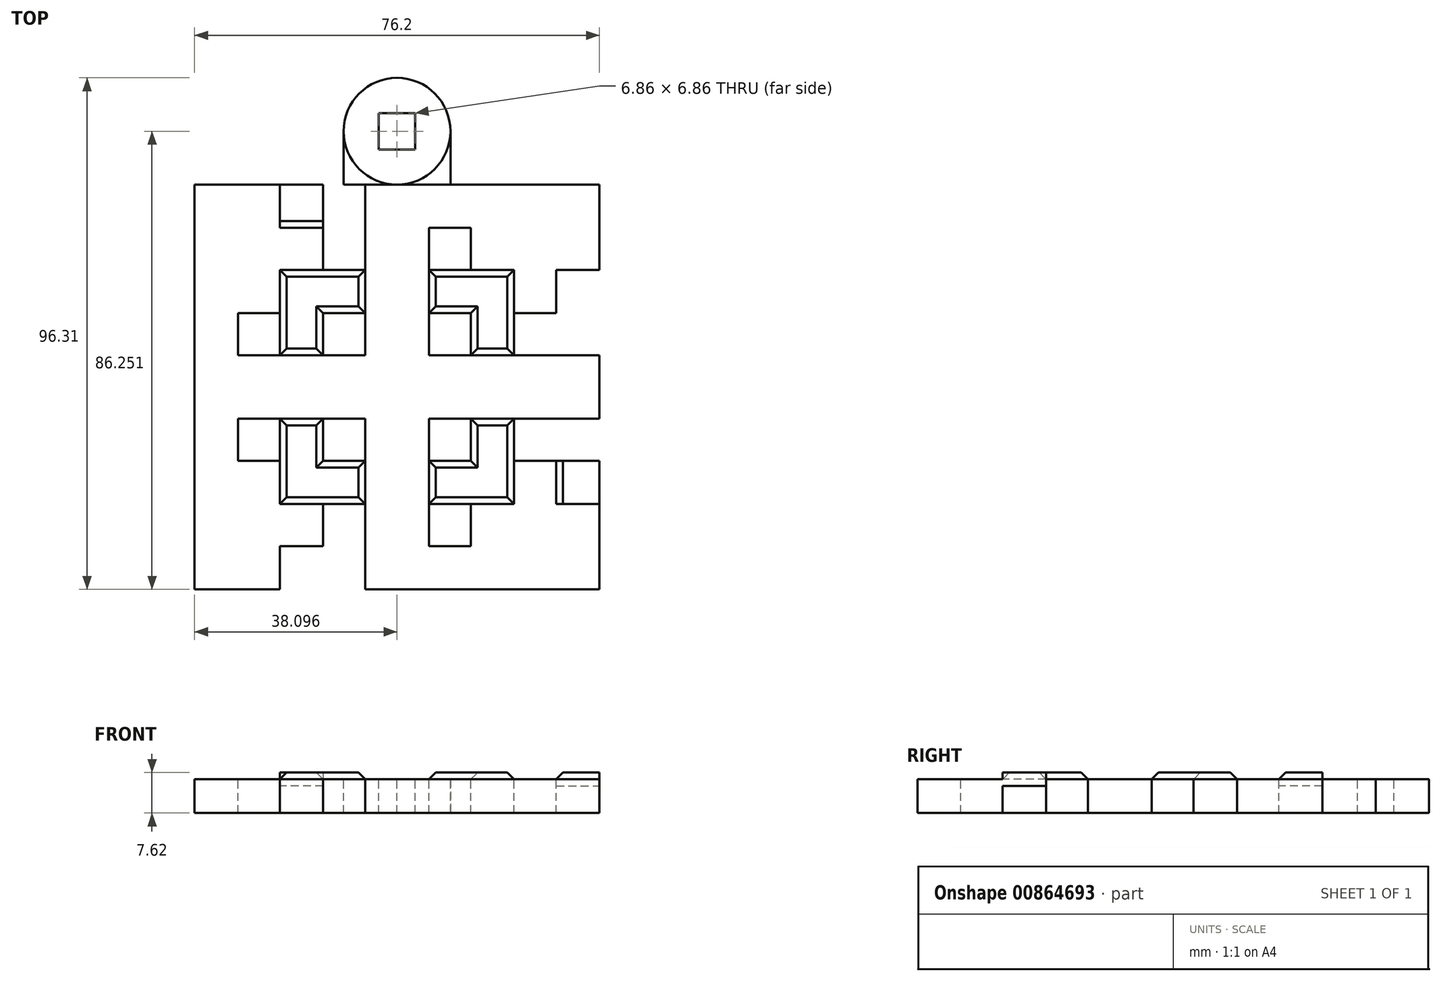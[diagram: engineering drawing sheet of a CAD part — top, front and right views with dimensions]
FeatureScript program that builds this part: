
annotation { "Feature Type Name" : "Feature", "Feature Type Description" : "" }
export const myFeature = defineFeature(function(context is Context, id is Id, definition is map)
    precondition{}
    {
        {
            var Q0;
            Q0=qCreatedBy(makeId("Top.planeOp"),FACE);
            var sketch = newSketch(context, id + "F0", { "sketchPlane" : qUnion([Q0])});
            skLineSegment(sketch, "E0.bottom", {"start": v(-34.48, 49.13) * mm, "end": v(41.72, 49.13) * mm});
            skLineSegment(sketch, "E0.top", {"start": v(-34.48, -27.07) * mm, "end": v(41.72, -27.07) * mm});
            skLineSegment(sketch, "E0.left", {"start": v(-34.48, 49.13) * mm, "end": v(-34.48, -27.07) * mm});
            skLineSegment(sketch, "E0.right", {"start": v(41.72, 49.13) * mm, "end": v(41.72, -27.07) * mm});
            skCircle(sketch, "E1", {"center": v(3.62, 59.18) * mm, "radius": 10.06 * mm});
            skLineSegment(sketch, "E2", {"start": v(3.62, -27.07) * mm, "end": v(3.62, 49.13) * mm, "construction": true});
            skPoint(sketch, "E3", {"position": v(3.62, 49.13) * mm});
            skSolve(sketch);
        }
        {
            var Q0;
            Q0 = qSketchRegion(id + "F0", true);
            extrude(context, id + "F1", {"entities" : qUnion([Q0]), "depth" : 6.35 * mm, "offsetDistance" : 25.4 * mm});
        }
        {
            var Q0;
            Q0=makeQuery(id+"F1.opExtrude","CAP_FACE",FACE,{"disambiguationData":[OSD([sQuery(id+"F0.wireOp",EDGE,"E0.bottom"),sQuery(id+"F0.wireOp",EDGE,"E0.top"),sQuery(id+"F0.wireOp",EDGE,"E0.left"),sQuery(id+"F0.wireOp",EDGE,"E0.right")])],"isStart":false});
            var sketch = newSketch(context, id + "F2", { "sketchPlane" : qUnion([Q0])});
            skLineSegment(sketch, "E4.bottom", {"start": v(-34.48, 5.04) * mm, "end": v(41.72, 5.04) * mm});
            skLineSegment(sketch, "E4.top", {"start": v(-34.48, 17.01) * mm, "end": v(41.72, 17.01) * mm});
            skLineSegment(sketch, "E4.left", {"start": v(-34.48, 5.04) * mm, "end": v(-34.48, 17.01) * mm});
            skLineSegment(sketch, "E4.right", {"start": v(41.72, 5.04) * mm, "end": v(41.72, 17.01) * mm});
            skLineSegment(sketch, "E5.bottom", {"start": v(-34.48, 49.13) * mm, "end": v(-2.37, 49.13) * mm});
            skLineSegment(sketch, "E5.top", {"start": v(-34.48, -27.07) * mm, "end": v(-2.37, -27.07) * mm});
            skLineSegment(sketch, "E5.left", {"start": v(-34.48, 49.13) * mm, "end": v(-34.48, 17.01) * mm});
            skLineSegment(sketch, "E5.right", {"start": v(41.72, 49.13) * mm, "end": v(41.72, 17.01) * mm});
            skLineSegment(sketch, "E6", {"start": v(41.72, 17.01) * mm, "end": v(41.72, 5.04) * mm});
            skLineSegment(sketch, "E7", {"start": v(41.72, 5.04) * mm, "end": v(41.72, -27.07) * mm});
            skLineSegment(sketch, "E8.bottom", {"start": v(-2.37, 49.13) * mm, "end": v(9.6, 49.13) * mm});
            skLineSegment(sketch, "E8.top", {"start": v(-2.37, -27.07) * mm, "end": v(9.6, -27.07) * mm});
            skLineSegment(sketch, "E8.left", {"start": v(-2.37, 49.13) * mm, "end": v(-2.37, 49.13) * mm});
            skLineSegment(sketch, "E8.right", {"start": v(9.6, 49.13) * mm, "end": v(9.6, -27.07) * mm});
            skLineSegment(sketch, "E9", {"start": v(-2.37, 49.13) * mm, "end": v(-2.37, -27.07) * mm});
            skLineSegment(sketch, "E10", {"start": v(9.6, 49.13) * mm, "end": v(41.72, 49.13) * mm});
            skLineSegment(sketch, "E11", {"start": v(9.6, -27.07) * mm, "end": v(41.72, -27.07) * mm});
            skPoint(sketch, "E12.oppositeSnap0", {"position": v(25.66, 49.13) * mm});
            skLineSegment(sketch, "E12.bottom", {"start": v(-18.43, 49.13) * mm, "end": v(25.66, 49.13) * mm});
            skLineSegment(sketch, "E12.top", {"start": v(-18.43, 40.98) * mm, "end": v(25.66, 40.98) * mm});
            skLineSegment(sketch, "E12.left", {"start": v(-18.43, 49.13) * mm, "end": v(-18.43, 40.98) * mm});
            skLineSegment(sketch, "E12.right", {"start": v(25.66, 49.13) * mm, "end": v(25.66, 40.98) * mm});
            skPoint(sketch, "E13.oppositeSnap0", {"position": v(-18.43, -27.07) * mm});
            skLineSegment(sketch, "E13.bottom", {"start": v(25.66, -27.07) * mm, "end": v(-18.43, -27.07) * mm});
            skLineSegment(sketch, "E13.top", {"start": v(25.66, -18.92) * mm, "end": v(-18.43, -18.92) * mm});
            skLineSegment(sketch, "E13.left", {"start": v(25.66, -27.07) * mm, "end": v(25.66, -18.92) * mm});
            skLineSegment(sketch, "E13.right", {"start": v(-18.43, -27.07) * mm, "end": v(-18.43, -18.92) * mm});
            skPoint(sketch, "E14.oppositeSnap0", {"position": v(41.72, 33.07) * mm});
            skLineSegment(sketch, "E14.bottom", {"start": v(41.72, -11.02) * mm, "end": v(33.57, -11.02) * mm});
            skLineSegment(sketch, "E14.top", {"start": v(41.72, 33.07) * mm, "end": v(33.57, 33.07) * mm});
            skLineSegment(sketch, "E14.left", {"start": v(41.72, -11.02) * mm, "end": v(41.72, 33.07) * mm});
            skLineSegment(sketch, "E14.right", {"start": v(33.57, -11.02) * mm, "end": v(33.57, 33.07) * mm});
            skLineSegment(sketch, "E15", {"start": v(-34.48, 17.01) * mm, "end": v(-34.48, 5.04) * mm});
            skLineSegment(sketch, "E16", {"start": v(-34.48, 5.04) * mm, "end": v(-34.48, -27.07) * mm});
            skPoint(sketch, "E17.oppositeSnap0", {"position": v(-34.48, -11.02) * mm});
            skLineSegment(sketch, "E17.bottom", {"start": v(-34.48, 33.07) * mm, "end": v(-26.33, 33.07) * mm});
            skLineSegment(sketch, "E17.top", {"start": v(-34.48, -11.02) * mm, "end": v(-26.33, -11.02) * mm});
            skLineSegment(sketch, "E17.left", {"start": v(-34.48, 33.07) * mm, "end": v(-34.48, -11.02) * mm});
            skLineSegment(sketch, "E17.right", {"start": v(-26.33, 33.07) * mm, "end": v(-26.33, 24.92) * mm});
            skLineSegment(sketch, "E18.bottom", {"start": v(-18.43, 40.98) * mm, "end": v(-10.28, 40.98) * mm});
            skLineSegment(sketch, "E18.top", {"start": v(-18.43, 17.01) * mm, "end": v(-10.28, 17.01) * mm});
            skLineSegment(sketch, "E18.left", {"start": v(-18.43, 40.98) * mm, "end": v(-18.43, 17.01) * mm});
            skLineSegment(sketch, "E18.right", {"start": v(-10.28, 40.98) * mm, "end": v(-10.28, 17.01) * mm});
            skLineSegment(sketch, "E19.bottom", {"start": v(-26.33, 33.07) * mm, "end": v(-2.37, 33.07) * mm});
            skLineSegment(sketch, "E19.top", {"start": v(-26.33, 24.92) * mm, "end": v(-2.37, 24.92) * mm});
            skLineSegment(sketch, "E19.right", {"start": v(-2.37, 33.07) * mm, "end": v(-2.37, 24.92) * mm});
            skLineSegment(sketch, "E20", {"start": v(-26.33, 24.92) * mm, "end": v(-26.33, -11.02) * mm});
            skLineSegment(sketch, "E21.bottom", {"start": v(25.66, 40.98) * mm, "end": v(17.51, 40.98) * mm});
            skLineSegment(sketch, "E21.top", {"start": v(25.66, 17.01) * mm, "end": v(17.51, 17.01) * mm});
            skLineSegment(sketch, "E21.left", {"start": v(25.66, 40.98) * mm, "end": v(25.66, 17.01) * mm});
            skLineSegment(sketch, "E21.right", {"start": v(17.51, 40.98) * mm, "end": v(17.51, 17.01) * mm});
            skLineSegment(sketch, "E22.bottom", {"start": v(33.57, 33.07) * mm, "end": v(9.6, 33.07) * mm});
            skLineSegment(sketch, "E22.top", {"start": v(33.57, 24.92) * mm, "end": v(9.6, 24.92) * mm});
            skLineSegment(sketch, "E22.left", {"start": v(33.57, 33.07) * mm, "end": v(33.57, 24.92) * mm});
            skLineSegment(sketch, "E22.right", {"start": v(9.6, 33.07) * mm, "end": v(9.6, 24.92) * mm});
            skPoint(sketch, "E23.oppositeSnap0", {"position": v(-10.28, 29) * mm});
            skLineSegment(sketch, "E23.bottom", {"start": v(-18.43, -18.92) * mm, "end": v(-10.28, -18.92) * mm});
            skLineSegment(sketch, "E23.top", {"start": v(-18.43, 5.04) * mm, "end": v(-10.28, 5.04) * mm});
            skLineSegment(sketch, "E23.left", {"start": v(-18.43, -18.92) * mm, "end": v(-18.43, 5.04) * mm});
            skLineSegment(sketch, "E23.right", {"start": v(-10.28, -18.92) * mm, "end": v(-10.28, 5.04) * mm});
            skLineSegment(sketch, "E24.bottom", {"start": v(25.66, -18.92) * mm, "end": v(17.51, -18.92) * mm});
            skLineSegment(sketch, "E24.top", {"start": v(25.66, 5.04) * mm, "end": v(17.51, 5.04) * mm});
            skLineSegment(sketch, "E24.left", {"start": v(25.66, -18.92) * mm, "end": v(25.66, 5.04) * mm});
            skLineSegment(sketch, "E24.right", {"start": v(17.51, -18.92) * mm, "end": v(17.51, 5.04) * mm});
            skLineSegment(sketch, "E25.bottom", {"start": v(-26.33, -11.02) * mm, "end": v(-2.37, -11.02) * mm});
            skLineSegment(sketch, "E25.top", {"start": v(-26.33, -2.87) * mm, "end": v(-2.37, -2.87) * mm});
            skLineSegment(sketch, "E25.left", {"start": v(-26.33, -11.02) * mm, "end": v(-26.33, -2.87) * mm});
            skLineSegment(sketch, "E25.right", {"start": v(-2.37, -11.02) * mm, "end": v(-2.37, -2.87) * mm});
            skLineSegment(sketch, "E26.bottom", {"start": v(9.6, -11.02) * mm, "end": v(33.57, -11.02) * mm});
            skLineSegment(sketch, "E26.top", {"start": v(9.6, -2.87) * mm, "end": v(33.57, -2.87) * mm});
            skLineSegment(sketch, "E26.left", {"start": v(9.6, -11.02) * mm, "end": v(9.6, -2.87) * mm});
            skLineSegment(sketch, "E26.right", {"start": v(33.57, -11.02) * mm, "end": v(33.57, -2.87) * mm});
            skLineSegment(sketch, "E27.bottom", {"start": v(-18.43, 49.13) * mm, "end": v(-10.28, 49.13) * mm});
            skLineSegment(sketch, "E27.right", {"start": v(-10.28, 49.13) * mm, "end": v(-10.28, 40.98) * mm});
            skLineSegment(sketch, "E28.bottom", {"start": v(17.51, 40.98) * mm, "end": v(25.66, 40.98) * mm});
            skLineSegment(sketch, "E28.top", {"start": v(17.51, 49.13) * mm, "end": v(25.66, 49.13) * mm});
            skLineSegment(sketch, "E28.left", {"start": v(17.51, 40.98) * mm, "end": v(17.51, 49.13) * mm});
            skLineSegment(sketch, "E28.right", {"start": v(25.66, 40.98) * mm, "end": v(25.66, 49.13) * mm});
            skLineSegment(sketch, "E29.bottom", {"start": v(33.57, 24.92) * mm, "end": v(41.72, 24.92) * mm});
            skLineSegment(sketch, "E29.top", {"start": v(33.57, 17.01) * mm, "end": v(41.72, 17.01) * mm});
            skLineSegment(sketch, "E29.left", {"start": v(33.57, 24.92) * mm, "end": v(33.57, 17.01) * mm});
            skLineSegment(sketch, "E29.right", {"start": v(41.72, 24.92) * mm, "end": v(41.72, 17.01) * mm});
            skLineSegment(sketch, "E30.bottom", {"start": v(-26.33, 24.92) * mm, "end": v(-34.48, 24.92) * mm});
            skLineSegment(sketch, "E30.top", {"start": v(-26.33, 33.07) * mm, "end": v(-34.48, 33.07) * mm});
            skLineSegment(sketch, "E30.left", {"start": v(-26.33, 24.92) * mm, "end": v(-26.33, 33.07) * mm});
            skLineSegment(sketch, "E30.right", {"start": v(-34.48, 24.92) * mm, "end": v(-34.48, 33.07) * mm});
            skLineSegment(sketch, "E31.top", {"start": v(-34.48, -2.87) * mm, "end": v(-26.33, -2.87) * mm});
            skLineSegment(sketch, "E31.left", {"start": v(-34.48, -11.02) * mm, "end": v(-34.48, -2.87) * mm});
            skLineSegment(sketch, "E32.top", {"start": v(-18.43, -27.07) * mm, "end": v(-10.28, -27.07) * mm});
            skLineSegment(sketch, "E32.left", {"start": v(-18.43, -18.92) * mm, "end": v(-18.43, -27.07) * mm});
            skLineSegment(sketch, "E32.right", {"start": v(-10.28, -18.92) * mm, "end": v(-10.28, -27.07) * mm});
            skLineSegment(sketch, "E33.bottom", {"start": v(17.51, -18.92) * mm, "end": v(25.66, -18.92) * mm});
            skLineSegment(sketch, "E33.top", {"start": v(17.51, -27.07) * mm, "end": v(25.66, -27.07) * mm});
            skLineSegment(sketch, "E33.left", {"start": v(17.51, -18.92) * mm, "end": v(17.51, -27.07) * mm});
            skLineSegment(sketch, "E33.right", {"start": v(25.66, -18.92) * mm, "end": v(25.66, -27.07) * mm});
            skLineSegment(sketch, "E34.bottom", {"start": v(33.57, -11.02) * mm, "end": v(41.72, -11.02) * mm});
            skLineSegment(sketch, "E34.top", {"start": v(33.57, -2.87) * mm, "end": v(41.72, -2.87) * mm});
            skLineSegment(sketch, "E34.right", {"start": v(41.72, -11.02) * mm, "end": v(41.72, -2.87) * mm});
            skSolve(sketch);
        }
        {
            var Q0;
            Q0=makeQuery(id+"F2.imprint","IMPRINT",FACE,{"disambiguationData":[TD([[makeQuery(id+"F2.imprint","IMPRINT",EDGE,{"derivedFrom":sQuery(id+"F2.wireOp",EDGE,"E5.bottom")}),-1.0]])]});
            var Q1;
            Q1=makeQuery(id+"F2.imprint","IMPRINT",FACE,{"disambiguationData":[TD([[makeQuery(id+"F2.imprint","IMPRINT",EDGE,{"derivedFrom":sQuery(id+"F2.wireOp",EDGE,"E5.right")}),-1.0]])]});
            var Q2;
            Q2=makeQuery(id+"F2.imprint","IMPRINT",FACE,{"disambiguationData":[TD([[makeQuery(id+"F2.imprint","IMPRINT",EDGE,{"derivedFrom":sQuery(id+"F2.wireOp",EDGE,"E7")}),-1.0]])]});
            var Q3;
            Q3=makeQuery(id+"F2.imprint","IMPRINT",FACE,{"disambiguationData":[TD([[makeQuery(id+"F2.imprint","IMPRINT",EDGE,{"derivedFrom":sQuery(id+"F2.wireOp",EDGE,"E5.top")}),1.0]])]});
            var Q4;
            {var subQ1=sQuery(id+"F2.wireOp",EDGE,"E4.bottom");var subQ3=sQuery(id+"F2.wireOp",EDGE,"E20");var subQ4=makeQuery(id+"F2.imprint","INTERSECT",VERTEX,{"derivedFrom":[subQ1,subQ3]});Q4=makeQuery(id+"F2.imprint","IMPRINT",FACE,{"disambiguationData":[TD([[makeQuery(id+"F2.imprint","IMPRINT",EDGE,{"disambiguationData":[TD([[subQ4,-1.0]])],"derivedFrom":subQ1}),-1.0]])]});}
            var Q5;
            {var subQ1=sQuery(id+"F2.wireOp",EDGE,"E4.top");var subQ3=sQuery(id+"F2.wireOp",EDGE,"E20");var subQ4=makeQuery(id+"F2.imprint","INTERSECT",VERTEX,{"derivedFrom":[subQ1,subQ3]});Q5=makeQuery(id+"F2.imprint","IMPRINT",FACE,{"disambiguationData":[TD([[makeQuery(id+"F2.imprint","IMPRINT",EDGE,{"disambiguationData":[TD([[subQ4,-1.0]])],"derivedFrom":subQ1}),1.0]])]});}
            var Q6;
            {var subQ1=sQuery(id+"F2.wireOp",EDGE,"E9");var subQ3=sQuery(id+"F2.wireOp",EDGE,"E12.top");var subQ4=makeQuery(id+"F2.imprint","INTERSECT",VERTEX,{"derivedFrom":[subQ1,subQ3]});Q6=makeQuery(id+"F2.imprint","IMPRINT",FACE,{"disambiguationData":[TD([[makeQuery(id+"F2.imprint","IMPRINT",EDGE,{"disambiguationData":[TD([[subQ4,-1.0]])],"derivedFrom":subQ1}),-1.0]])]});}
            var Q7;
            {var subQ1=sQuery(id+"F2.wireOp",EDGE,"E4.top");var subQ3=sQuery(id+"F2.wireOp",EDGE,"E9");var subQ4=makeQuery(id+"F2.imprint","INTERSECT",VERTEX,{"derivedFrom":[subQ1,subQ3]});Q7=makeQuery(id+"F2.imprint","IMPRINT",FACE,{"disambiguationData":[TD([[makeQuery(id+"F2.imprint","IMPRINT",EDGE,{"disambiguationData":[TD([[subQ4,1.0]])],"derivedFrom":subQ1}),1.0]])]});}
            var Q8;
            {var subQ1=sQuery(id+"F2.wireOp",EDGE,"E4.bottom");var subQ3=sQuery(id+"F2.wireOp",EDGE,"E9");var subQ4=makeQuery(id+"F2.imprint","INTERSECT",VERTEX,{"derivedFrom":[subQ1,subQ3]});Q8=makeQuery(id+"F2.imprint","IMPRINT",FACE,{"disambiguationData":[TD([[makeQuery(id+"F2.imprint","IMPRINT",EDGE,{"disambiguationData":[TD([[subQ4,1.0]])],"derivedFrom":subQ1}),-1.0]])]});}
            var Q9;
            {var subQ1=sQuery(id+"F2.wireOp",EDGE,"E9");var subQ3=sQuery(id+"F2.wireOp",EDGE,"E13.top");var subQ4=makeQuery(id+"F2.imprint","INTERSECT",VERTEX,{"derivedFrom":[subQ1,subQ3]});Q9=makeQuery(id+"F2.imprint","IMPRINT",FACE,{"disambiguationData":[TD([[makeQuery(id+"F2.imprint","IMPRINT",EDGE,{"disambiguationData":[TD([[subQ4,1.0]])],"derivedFrom":subQ1}),-1.0]])]});}
            var Q10;
            {var subQ1=sQuery(id+"F2.wireOp",EDGE,"E8.right");var subQ3=sQuery(id+"F2.wireOp",EDGE,"E13.top");var subQ4=makeQuery(id+"F2.imprint","INTERSECT",VERTEX,{"derivedFrom":[subQ1,subQ3]});Q10=makeQuery(id+"F2.imprint","IMPRINT",FACE,{"disambiguationData":[TD([[makeQuery(id+"F2.imprint","IMPRINT",EDGE,{"disambiguationData":[TD([[subQ4,1.0]])],"derivedFrom":subQ1}),1.0]])]});}
            var Q11;
            {var subQ1=sQuery(id+"F2.wireOp",EDGE,"E4.bottom");var subQ3=sQuery(id+"F2.wireOp",EDGE,"E8.right");var subQ4=makeQuery(id+"F2.imprint","INTERSECT",VERTEX,{"derivedFrom":[subQ1,subQ3]});Q11=makeQuery(id+"F2.imprint","IMPRINT",FACE,{"disambiguationData":[TD([[makeQuery(id+"F2.imprint","IMPRINT",EDGE,{"disambiguationData":[TD([[subQ4,-1.0]])],"derivedFrom":subQ1}),-1.0]])]});}
            var Q12;
            {var subQ1=sQuery(id+"F2.wireOp",EDGE,"E4.bottom");var subQ3=sQuery(id+"F2.wireOp",EDGE,"E14.right");var subQ4=makeQuery(id+"F2.imprint","INTERSECT",VERTEX,{"derivedFrom":[subQ1,subQ3]});Q12=makeQuery(id+"F2.imprint","IMPRINT",FACE,{"disambiguationData":[TD([[makeQuery(id+"F2.imprint","IMPRINT",EDGE,{"disambiguationData":[TD([[subQ4,1.0]])],"derivedFrom":subQ1}),-1.0]])]});}
            var Q13;
            {var subQ1=sQuery(id+"F2.wireOp",EDGE,"E4.top");var subQ3=sQuery(id+"F2.wireOp",EDGE,"E14.right");var subQ4=makeQuery(id+"F2.imprint","INTERSECT",VERTEX,{"derivedFrom":[subQ1,subQ3]});Q13=makeQuery(id+"F2.imprint","IMPRINT",FACE,{"disambiguationData":[TD([[makeQuery(id+"F2.imprint","IMPRINT",EDGE,{"disambiguationData":[TD([[subQ4,1.0]])],"derivedFrom":subQ1}),1.0]])]});}
            var Q14;
            {var subQ1=sQuery(id+"F2.wireOp",EDGE,"E4.top");var subQ3=sQuery(id+"F2.wireOp",EDGE,"E8.right");var subQ4=makeQuery(id+"F2.imprint","INTERSECT",VERTEX,{"derivedFrom":[subQ1,subQ3]});Q14=makeQuery(id+"F2.imprint","IMPRINT",FACE,{"disambiguationData":[TD([[makeQuery(id+"F2.imprint","IMPRINT",EDGE,{"disambiguationData":[TD([[subQ4,-1.0]])],"derivedFrom":subQ1}),1.0]])]});}
            var Q15;
            {var subQ1=sQuery(id+"F2.wireOp",EDGE,"E8.right");var subQ3=sQuery(id+"F2.wireOp",EDGE,"E12.top");var subQ4=makeQuery(id+"F2.imprint","INTERSECT",VERTEX,{"derivedFrom":[subQ1,subQ3]});Q15=makeQuery(id+"F2.imprint","IMPRINT",FACE,{"disambiguationData":[TD([[makeQuery(id+"F2.imprint","IMPRINT",EDGE,{"disambiguationData":[TD([[subQ4,-1.0]])],"derivedFrom":subQ1}),1.0]])]});}
            var Q16;
            Q16 = qSketchRegion(id + "F6", true);
            extrude(context, id + "F3", {"entities" : qUnion([Q0, Q1, Q2, Q3, Q4, Q5, Q6, Q7, Q8, Q9, Q10, Q11, Q12, Q13, Q14, Q15, Q16]), "operationType" : NewBodyOperationType.REMOVE, "oppositeDirection" : true, "depth" : 25.4 * mm, "offsetDistance" : 25.4 * mm});
        }
        {
            var Q0;
            Q0=makeQuery(id+"F1.opExtrude","CAP_FACE",FACE,{"disambiguationData":[OSD([sQuery(id+"F0.wireOp",EDGE,"E1")])],"isStart":false});
            var sketch = newSketch(context, id + "F4", { "sketchPlane" : qUnion([Q0])});
            skLineSegment(sketch, "E35.bottom", {"start": v(7.04, 55.75) * mm, "end": v(0.19, 55.75) * mm});
            skLineSegment(sketch, "E35.top", {"start": v(7.04, 62.61) * mm, "end": v(0.19, 62.61) * mm});
            skLineSegment(sketch, "E35.left", {"start": v(7.04, 55.75) * mm, "end": v(7.04, 62.61) * mm});
            skLineSegment(sketch, "E35.right", {"start": v(0.19, 55.75) * mm, "end": v(0.19, 62.61) * mm});
            skPoint(sketch, "E35.middle", {"position": v(3.62, 59.18) * mm});
            skSolve(sketch);
        }
        {
            var Q0;
            Q0=makeQuery(id+"F4.imprint","IMPRINT",FACE,{"disambiguationData":[TD([[makeQuery(id+"F4.imprint","IMPRINT",EDGE,{"derivedFrom":sQuery(id+"F4.wireOp",EDGE,"E35.bottom")}),-1.0]])]});
            var Q1;
            Q1 = qSketchRegion(id + "F6", true);
            extrude(context, id + "F5", {"entities" : qUnion([Q0, Q1]), "operationType" : NewBodyOperationType.REMOVE, "oppositeDirection" : true, "depth" : 25.4 * mm, "offsetDistance" : 25.4 * mm});
        }
        {
            var Q0;
            Q0=makeQuery(id+"F1.opExtrude","CAP_FACE",FACE,{"disambiguationData":[OSD([sQuery(id+"F0.wireOp",EDGE,"E0.bottom"),sQuery(id+"F0.wireOp",EDGE,"E0.top"),sQuery(id+"F0.wireOp",EDGE,"E0.left"),sQuery(id+"F0.wireOp",EDGE,"E0.right")])],"isStart":false});
            var sketch = newSketch(context, id + "F6", { "sketchPlane" : qUnion([Q0])});
            skLineSegment(sketch, "E36.bottom", {"start": v(-26.33, 24.92) * mm, "end": v(-34.48, 24.92) * mm});
            skLineSegment(sketch, "E36.top", {"start": v(-26.33, 33.07) * mm, "end": v(-34.48, 33.07) * mm});
            skLineSegment(sketch, "E36.left", {"start": v(-26.33, 24.92) * mm, "end": v(-26.33, 33.07) * mm});
            skLineSegment(sketch, "E36.right", {"start": v(-34.48, 24.92) * mm, "end": v(-34.48, 33.07) * mm});
            skLineSegment(sketch, "E37.bottom", {"start": v(-26.33, -2.87) * mm, "end": v(-34.48, -2.87) * mm});
            skLineSegment(sketch, "E37.top", {"start": v(-26.33, -11.02) * mm, "end": v(-34.48, -11.02) * mm});
            skLineSegment(sketch, "E37.left", {"start": v(-26.33, -2.87) * mm, "end": v(-26.33, -11.02) * mm});
            skLineSegment(sketch, "E37.right", {"start": v(-34.48, -2.87) * mm, "end": v(-34.48, -11.02) * mm});
            skLineSegment(sketch, "E38.bottom", {"start": v(-10.28, 40.98) * mm, "end": v(-18.43, 40.98) * mm});
            skLineSegment(sketch, "E38.top", {"start": v(-10.28, 49.13) * mm, "end": v(-18.43, 49.13) * mm});
            skLineSegment(sketch, "E38.left", {"start": v(-10.28, 40.98) * mm, "end": v(-10.28, 49.13) * mm});
            skLineSegment(sketch, "E38.right", {"start": v(-18.43, 40.98) * mm, "end": v(-18.43, 49.13) * mm});
            skLineSegment(sketch, "E39.bottom", {"start": v(17.51, 40.98) * mm, "end": v(25.66, 40.98) * mm});
            skLineSegment(sketch, "E39.top", {"start": v(17.51, 49.13) * mm, "end": v(25.66, 49.13) * mm});
            skLineSegment(sketch, "E39.left", {"start": v(17.51, 40.98) * mm, "end": v(17.51, 49.13) * mm});
            skLineSegment(sketch, "E39.right", {"start": v(25.66, 40.98) * mm, "end": v(25.66, 49.13) * mm});
            skLineSegment(sketch, "E40.bottom", {"start": v(33.57, 24.92) * mm, "end": v(41.72, 24.92) * mm});
            skLineSegment(sketch, "E40.top", {"start": v(33.57, 33.07) * mm, "end": v(41.72, 33.07) * mm});
            skLineSegment(sketch, "E40.left", {"start": v(33.57, 24.92) * mm, "end": v(33.57, 33.07) * mm});
            skLineSegment(sketch, "E40.right", {"start": v(41.72, 24.92) * mm, "end": v(41.72, 33.07) * mm});
            skLineSegment(sketch, "E41.bottom", {"start": v(33.57, -2.87) * mm, "end": v(41.72, -2.87) * mm});
            skLineSegment(sketch, "E41.top", {"start": v(33.57, -11.02) * mm, "end": v(41.72, -11.02) * mm});
            skLineSegment(sketch, "E41.left", {"start": v(33.57, -2.87) * mm, "end": v(33.57, -11.02) * mm});
            skLineSegment(sketch, "E41.right", {"start": v(41.72, -2.87) * mm, "end": v(41.72, -11.02) * mm});
            skLineSegment(sketch, "E42.bottom", {"start": v(17.51, -18.92) * mm, "end": v(25.66, -18.92) * mm});
            skLineSegment(sketch, "E42.top", {"start": v(17.51, -27.07) * mm, "end": v(25.66, -27.07) * mm});
            skLineSegment(sketch, "E42.left", {"start": v(17.51, -18.92) * mm, "end": v(17.51, -27.07) * mm});
            skLineSegment(sketch, "E42.right", {"start": v(25.66, -18.92) * mm, "end": v(25.66, -27.07) * mm});
            skLineSegment(sketch, "E43.bottom", {"start": v(-10.28, -18.92) * mm, "end": v(-18.43, -18.92) * mm});
            skLineSegment(sketch, "E43.top", {"start": v(-10.28, -27.07) * mm, "end": v(-18.43, -27.07) * mm});
            skLineSegment(sketch, "E43.left", {"start": v(-10.28, -18.92) * mm, "end": v(-10.28, -27.07) * mm});
            skLineSegment(sketch, "E43.right", {"start": v(-18.43, -18.92) * mm, "end": v(-18.43, -27.07) * mm});
            skLineSegment(sketch, "E44.bottom", {"start": v(-26.33, 33.07) * mm, "end": v(-2.37, 33.07) * mm});
            skLineSegment(sketch, "E44.top", {"start": v(-26.33, 24.92) * mm, "end": v(-2.37, 24.92) * mm});
            skLineSegment(sketch, "E44.left", {"start": v(-26.33, 33.07) * mm, "end": v(-26.33, 24.92) * mm});
            skLineSegment(sketch, "E44.right", {"start": v(-2.37, 33.07) * mm, "end": v(-2.37, 24.92) * mm});
            skLineSegment(sketch, "E45.top", {"start": v(-10.28, 17.01) * mm, "end": v(-18.43, 17.01) * mm});
            skLineSegment(sketch, "E45.left", {"start": v(-10.28, 40.98) * mm, "end": v(-10.28, 17.01) * mm});
            skLineSegment(sketch, "E45.right", {"start": v(-18.43, 40.98) * mm, "end": v(-18.43, 17.01) * mm});
            skLineSegment(sketch, "E46.bottom", {"start": v(-18.43, 5.04) * mm, "end": v(-10.28, 5.04) * mm});
            skLineSegment(sketch, "E46.top", {"start": v(-18.43, -18.92) * mm, "end": v(-10.28, -18.92) * mm});
            skLineSegment(sketch, "E46.left", {"start": v(-18.43, 5.04) * mm, "end": v(-18.43, -18.92) * mm});
            skLineSegment(sketch, "E46.right", {"start": v(-10.28, 5.04) * mm, "end": v(-10.28, -18.92) * mm});
            skLineSegment(sketch, "E47.bottom", {"start": v(-26.33, -11.02) * mm, "end": v(-2.37, -11.02) * mm});
            skLineSegment(sketch, "E47.top", {"start": v(-26.33, -2.87) * mm, "end": v(-2.37, -2.87) * mm});
            skLineSegment(sketch, "E47.left", {"start": v(-26.33, -11.02) * mm, "end": v(-26.33, -2.87) * mm});
            skLineSegment(sketch, "E47.right", {"start": v(-2.37, -11.02) * mm, "end": v(-2.37, -2.87) * mm});
            skLineSegment(sketch, "E48.bottom", {"start": v(9.6, -2.87) * mm, "end": v(33.57, -2.87) * mm});
            skLineSegment(sketch, "E48.top", {"start": v(9.6, -11.02) * mm, "end": v(33.57, -11.02) * mm});
            skLineSegment(sketch, "E48.left", {"start": v(9.6, -2.87) * mm, "end": v(9.6, -11.02) * mm});
            skLineSegment(sketch, "E49.bottom", {"start": v(25.66, -18.92) * mm, "end": v(17.51, -18.92) * mm});
            skLineSegment(sketch, "E49.top", {"start": v(25.66, 5.04) * mm, "end": v(17.51, 5.04) * mm});
            skLineSegment(sketch, "E49.left", {"start": v(25.66, -18.92) * mm, "end": v(25.66, 5.04) * mm});
            skLineSegment(sketch, "E49.right", {"start": v(17.51, -18.92) * mm, "end": v(17.51, 5.04) * mm});
            skLineSegment(sketch, "E50.bottom", {"start": v(17.51, 17.01) * mm, "end": v(25.66, 17.01) * mm});
            skLineSegment(sketch, "E50.left", {"start": v(17.51, 17.01) * mm, "end": v(17.51, 40.98) * mm});
            skLineSegment(sketch, "E50.right", {"start": v(25.66, 17.01) * mm, "end": v(25.66, 40.98) * mm});
            skLineSegment(sketch, "E51.bottom", {"start": v(9.6, 33.07) * mm, "end": v(33.57, 33.07) * mm});
            skLineSegment(sketch, "E51.top", {"start": v(9.6, 24.92) * mm, "end": v(33.57, 24.92) * mm});
            skLineSegment(sketch, "E51.left", {"start": v(9.6, 33.07) * mm, "end": v(9.6, 24.92) * mm});
            skLineSegment(sketch, "E51.right", {"start": v(33.57, 33.07) * mm, "end": v(33.57, 24.92) * mm});
            skSolve(sketch);
        }
        {
            var Q0;
            {var subQ3=sQuery(id+"F6.wireOp",EDGE,"E44.left");Q0=makeQuery(id+"F6.imprint","IMPRINT",FACE,{"disambiguationData":[TD([[makeQuery(id+"F6.imprint","IMPRINT",EDGE,{"derivedFrom":subQ3}),1.0]])]});}
            var Q1;
            {var subQ1=sQuery(id+"F6.wireOp",EDGE,"E44.bottom");var subQ3=sQuery(id+"F6.wireOp",EDGE,"E45.left");var subQ4=makeQuery(id+"F6.imprint","INTERSECT",VERTEX,{"derivedFrom":[subQ1,subQ3]});Q1=makeQuery(id+"F6.imprint","IMPRINT",FACE,{"disambiguationData":[TD([[makeQuery(id+"F6.imprint","IMPRINT",EDGE,{"disambiguationData":[TD([[subQ4,1.0]])],"derivedFrom":subQ1}),-1.0]])]});}
            var Q2;
            {var subQ5=sQuery(id+"F6.wireOp",EDGE,"E38.bottom");Q2=makeQuery(id+"F6.imprint","IMPRINT",FACE,{"disambiguationData":[TD([[makeQuery(id+"F6.imprint","IMPRINT",EDGE,{"derivedFrom":subQ5}),1.0]])]});}
            var Q3;
            {var subQ0=sQuery(id+"F6.wireOp",EDGE,"E44.right");Q3=makeQuery(id+"F6.imprint","IMPRINT",FACE,{"disambiguationData":[TD([[makeQuery(id+"F6.imprint","IMPRINT",EDGE,{"derivedFrom":subQ0}),-1.0]])]});}
            var Q4;
            {var subQ5=sQuery(id+"F6.wireOp",EDGE,"E45.top");Q4=makeQuery(id+"F6.imprint","IMPRINT",FACE,{"disambiguationData":[TD([[makeQuery(id+"F6.imprint","IMPRINT",EDGE,{"derivedFrom":subQ5}),-1.0]])]});}
            var Q5;
            {var subQ5=sQuery(id+"F6.wireOp",EDGE,"E51.left");Q5=makeQuery(id+"F6.imprint","IMPRINT",FACE,{"disambiguationData":[TD([[makeQuery(id+"F6.imprint","IMPRINT",EDGE,{"derivedFrom":subQ5}),1.0]])]});}
            var Q6;
            {var subQ5=sQuery(id+"F6.wireOp",EDGE,"E51.right");Q6=makeQuery(id+"F6.imprint","IMPRINT",FACE,{"disambiguationData":[TD([[makeQuery(id+"F6.imprint","IMPRINT",EDGE,{"derivedFrom":subQ5}),-1.0]])]});}
            var Q7;
            {var subQ0=sQuery(id+"F6.wireOp",EDGE,"E51.bottom");var subQ1=sQuery(id+"F6.wireOp",EDGE,"E50.left");var subQ2=makeQuery(id+"F6.imprint","INTERSECT",VERTEX,{"derivedFrom":[subQ1,subQ0]});var subQ3=sQuery(id+"F6.wireOp",EDGE,"E51.top");var subQ4=makeQuery(id+"F6.imprint","INTERSECT",VERTEX,{"derivedFrom":[subQ1,subQ3]});Q7=makeQuery(id+"F6.imprint","IMPRINT",FACE,{"disambiguationData":[TD([[makeQuery(id+"F6.imprint","IMPRINT",EDGE,{"disambiguationData":[TD([[subQ2,1.0],[subQ4,-1.0]])],"derivedFrom":subQ1}),-1.0]])]});}
            var Q8;
            {var subQ0=sQuery(id+"F6.wireOp",EDGE,"E39.bottom");Q8=makeQuery(id+"F6.imprint","IMPRINT",FACE,{"disambiguationData":[TD([[makeQuery(id+"F6.imprint","IMPRINT",EDGE,{"derivedFrom":subQ0}),-1.0]])]});}
            var Q9;
            {var subQ0=sQuery(id+"F6.wireOp",EDGE,"E50.bottom");Q9=makeQuery(id+"F6.imprint","IMPRINT",FACE,{"disambiguationData":[TD([[makeQuery(id+"F6.imprint","IMPRINT",EDGE,{"derivedFrom":subQ0}),1.0]])]});}
            var Q10;
            {var subQ0=sQuery(id+"F6.wireOp",EDGE,"E46.bottom");Q10=makeQuery(id+"F6.imprint","IMPRINT",FACE,{"disambiguationData":[TD([[makeQuery(id+"F6.imprint","IMPRINT",EDGE,{"derivedFrom":subQ0}),-1.0]])]});}
            var Q11;
            {var subQ0=sQuery(id+"F6.wireOp",EDGE,"E47.bottom");var subQ1=sQuery(id+"F6.wireOp",EDGE,"E46.left");var subQ2=makeQuery(id+"F6.imprint","INTERSECT",VERTEX,{"derivedFrom":[subQ1,subQ0]});Q11=makeQuery(id+"F6.imprint","IMPRINT",FACE,{"disambiguationData":[TD([[makeQuery(id+"F6.imprint","IMPRINT",EDGE,{"disambiguationData":[TD([[subQ2,1.0]])],"derivedFrom":subQ1}),1.0]])]});}
            var Q12;
            {var subQ0=sQuery(id+"F6.wireOp",EDGE,"E46.top");Q12=makeQuery(id+"F6.imprint","IMPRINT",FACE,{"disambiguationData":[TD([[makeQuery(id+"F6.imprint","IMPRINT",EDGE,{"derivedFrom":subQ0}),1.0]])]});}
            var Q13;
            {var subQ5=sQuery(id+"F6.wireOp",EDGE,"E47.left");Q13=makeQuery(id+"F6.imprint","IMPRINT",FACE,{"disambiguationData":[TD([[makeQuery(id+"F6.imprint","IMPRINT",EDGE,{"derivedFrom":subQ5}),-1.0]])]});}
            var Q14;
            {var subQ5=sQuery(id+"F6.wireOp",EDGE,"E47.right");Q14=makeQuery(id+"F6.imprint","IMPRINT",FACE,{"disambiguationData":[TD([[makeQuery(id+"F6.imprint","IMPRINT",EDGE,{"derivedFrom":subQ5}),1.0]])]});}
            var Q15;
            {var subQ0=sQuery(id+"F6.wireOp",EDGE,"E48.left");Q15=makeQuery(id+"F6.imprint","IMPRINT",FACE,{"disambiguationData":[TD([[makeQuery(id+"F6.imprint","IMPRINT",EDGE,{"derivedFrom":subQ0}),1.0]])]});}
            var Q16;
            {var subQ0=sQuery(id+"F6.wireOp",EDGE,"E49.left");var subQ1=sQuery(id+"F6.wireOp",EDGE,"E48.bottom");var subQ2=makeQuery(id+"F6.imprint","INTERSECT",VERTEX,{"derivedFrom":[subQ1,subQ0]});Q16=makeQuery(id+"F6.imprint","IMPRINT",FACE,{"disambiguationData":[TD([[makeQuery(id+"F6.imprint","IMPRINT",EDGE,{"disambiguationData":[TD([[subQ2,1.0]])],"derivedFrom":subQ1}),-1.0]])]});}
            var Q17;
            {var subQ0=sQuery(id+"F6.wireOp",EDGE,"E41.left");Q17=makeQuery(id+"F6.imprint","IMPRINT",FACE,{"disambiguationData":[TD([[makeQuery(id+"F6.imprint","IMPRINT",EDGE,{"derivedFrom":subQ0}),-1.0]])]});}
            var Q18;
            {var subQ5=sQuery(id+"F6.wireOp",EDGE,"E49.bottom");Q18=makeQuery(id+"F6.imprint","IMPRINT",FACE,{"disambiguationData":[TD([[makeQuery(id+"F6.imprint","IMPRINT",EDGE,{"derivedFrom":subQ5}),-1.0]])]});}
            var Q19;
            {var subQ5=sQuery(id+"F6.wireOp",EDGE,"E49.top");Q19=makeQuery(id+"F6.imprint","IMPRINT",FACE,{"disambiguationData":[TD([[makeQuery(id+"F6.imprint","IMPRINT",EDGE,{"derivedFrom":subQ5}),1.0]])]});}
            extrude(context, id + "F7", {"entities" : qUnion([Q0, Q1, Q2, Q3, Q4, Q5, Q6, Q7, Q8, Q9, Q10, Q11, Q12, Q13, Q14, Q15, Q16, Q17, Q18, Q19]), "operationType" : NewBodyOperationType.ADD, "depth" : 2.54 * mm, "offsetDistance" : 25.4 * mm, "symmetric" : true});
        }
        {
            var Q0;
            {var subQ0=sQuery(id+"F6.wireOp",EDGE,"E44.bottom");Q0=makeQuery(id+"F7.opExtrude","CAP_EDGE",EDGE,{"disambiguationData":[OSD([subQ0]),TDD([makeQuery(id+"F6.imprint","IMPRINT",EDGE,{"disambiguationData":[TD([[makeQuery(id+"F6.imprint","INTERSECT",VERTEX,{"derivedFrom":[sQuery(id+"F6.wireOp",EDGE,"E36.top"),subQ0,sQuery(id+"F6.wireOp",EDGE,"E44.left")]}),1.0]])],"derivedFrom":subQ0})])],"isStart":false});}
            var Q1;
            {var subQ0=sQuery(id+"F6.wireOp",EDGE,"E45.right");Q1=makeQuery(id+"F7.opExtrude","CAP_EDGE",EDGE,{"disambiguationData":[OSD([subQ0]),TDD([makeQuery(id+"F6.imprint","IMPRINT",EDGE,{"disambiguationData":[TD([[makeQuery(id+"F6.imprint","INTERSECT",VERTEX,{"derivedFrom":[sQuery(id+"F6.wireOp",EDGE,"E44.bottom"),subQ0]}),1.0]])],"derivedFrom":subQ0})])],"isStart":false});}
            var Q2;
            Q2=makeQuery(id+"F7.opExtrude","CAP_EDGE",EDGE,{"disambiguationData":[OSD([sQuery(id+"F6.wireOp",EDGE,"E38.bottom")])],"isStart":false});
            var Q3;
            {var subQ0=sQuery(id+"F6.wireOp",EDGE,"E45.left");Q3=makeQuery(id+"F7.opExtrude","CAP_EDGE",EDGE,{"disambiguationData":[OSD([subQ0]),TDD([makeQuery(id+"F6.imprint","IMPRINT",EDGE,{"disambiguationData":[TD([[makeQuery(id+"F6.imprint","INTERSECT",VERTEX,{"derivedFrom":[sQuery(id+"F6.wireOp",EDGE,"E44.bottom"),subQ0]}),1.0]])],"derivedFrom":subQ0})])],"isStart":false});}
            var Q4;
            {var subQ0=sQuery(id+"F6.wireOp",EDGE,"E44.bottom");Q4=makeQuery(id+"F7.opExtrude","CAP_EDGE",EDGE,{"disambiguationData":[OSD([subQ0]),TDD([makeQuery(id+"F6.imprint","IMPRINT",EDGE,{"disambiguationData":[TD([[makeQuery(id+"F6.imprint","INTERSECT",VERTEX,{"derivedFrom":[subQ0,sQuery(id+"F6.wireOp",EDGE,"E45.left")]}),-1.0]])],"derivedFrom":subQ0})])],"isStart":false});}
            var Q5;
            Q5=makeQuery(id+"F7.opExtrude","CAP_EDGE",EDGE,{"disambiguationData":[OSD([sQuery(id+"F6.wireOp",EDGE,"E44.right")])],"isStart":false});
            var Q6;
            {var subQ0=sQuery(id+"F6.wireOp",EDGE,"E44.top");Q6=makeQuery(id+"F7.opExtrude","CAP_EDGE",EDGE,{"disambiguationData":[OSD([subQ0]),TDD([makeQuery(id+"F6.imprint","IMPRINT",EDGE,{"disambiguationData":[TD([[makeQuery(id+"F6.imprint","INTERSECT",VERTEX,{"derivedFrom":[subQ0,sQuery(id+"F6.wireOp",EDGE,"E45.left")]}),-1.0]])],"derivedFrom":subQ0})])],"isStart":false});}
            var Q7;
            {var subQ0=sQuery(id+"F6.wireOp",EDGE,"E45.left");Q7=makeQuery(id+"F7.opExtrude","CAP_EDGE",EDGE,{"disambiguationData":[OSD([subQ0]),TDD([makeQuery(id+"F6.imprint","IMPRINT",EDGE,{"disambiguationData":[TD([[makeQuery(id+"F6.imprint","INTERSECT",VERTEX,{"derivedFrom":[sQuery(id+"F6.wireOp",EDGE,"E44.top"),subQ0]}),-1.0]])],"derivedFrom":subQ0})])],"isStart":false});}
            var Q8;
            Q8=makeQuery(id+"F7.opExtrude","CAP_EDGE",EDGE,{"disambiguationData":[OSD([sQuery(id+"F6.wireOp",EDGE,"E45.top")])],"isStart":false});
            var Q9;
            {var subQ0=sQuery(id+"F6.wireOp",EDGE,"E45.right");Q9=makeQuery(id+"F7.opExtrude","CAP_EDGE",EDGE,{"disambiguationData":[OSD([subQ0]),TDD([makeQuery(id+"F6.imprint","IMPRINT",EDGE,{"disambiguationData":[TD([[makeQuery(id+"F6.imprint","INTERSECT",VERTEX,{"derivedFrom":[sQuery(id+"F6.wireOp",EDGE,"E44.top"),subQ0]}),-1.0]])],"derivedFrom":subQ0})])],"isStart":false});}
            var Q10;
            {var subQ0=sQuery(id+"F6.wireOp",EDGE,"E44.top");Q10=makeQuery(id+"F7.opExtrude","CAP_EDGE",EDGE,{"disambiguationData":[OSD([subQ0]),TDD([makeQuery(id+"F6.imprint","IMPRINT",EDGE,{"disambiguationData":[TD([[makeQuery(id+"F6.imprint","INTERSECT",VERTEX,{"derivedFrom":[subQ0,sQuery(id+"F6.wireOp",EDGE,"E45.right")]}),1.0]])],"derivedFrom":subQ0})])],"isStart":false});}
            var Q11;
            Q11=makeQuery(id+"F7.opExtrude","CAP_EDGE",EDGE,{"disambiguationData":[OSD([sQuery(id+"F6.wireOp",EDGE,"E44.left")])],"isStart":false});
            var Q12;
            {var subQ0=sQuery(id+"F6.wireOp",EDGE,"E46.right");var subQ1=sQuery(id+"F2.wireOp",EDGE,"E4.bottom");Q12=makeQuery(id+"F7.opExtrude","CAP_EDGE",EDGE,{"disambiguationData":[OSD([subQ0]),TDD([makeQuery(id+"F6.imprint","IMPRINT",EDGE,{"disambiguationData":[TD([[makeQuery(id+"F6.imprint","INTERSECT",VERTEX,{"derivedFrom":[makeQuery(id+"F3.boolean.opBoolean","COPY",EDGE,{"derivedFrom":makeQuery(id+"F3.opExtrude","CAP_EDGE",EDGE,{"disambiguationData":[OSD([subQ1]),TDD([makeQuery(id+"F2.imprint","IMPRINT",EDGE,{"disambiguationData":[TD([[makeQuery(id+"F2.imprint","INTERSECT",VERTEX,{"derivedFrom":[subQ1,sQuery(id+"F2.wireOp",EDGE,"E9")]}),1.0]])],"derivedFrom":subQ1})])],"isStart":true})}),sQuery(id+"F6.wireOp",EDGE,"E46.bottom"),subQ0]}),1.0],[makeQuery(id+"F6.imprint","INTERSECT",VERTEX,{"derivedFrom":[subQ0,sQuery(id+"F6.wireOp",EDGE,"E47.top")]}),-1.0]])],"derivedFrom":subQ0})])],"isStart":false});}
            var Q13;
            {var subQ0=sQuery(id+"F6.wireOp",EDGE,"E47.top");Q13=makeQuery(id+"F7.opExtrude","CAP_EDGE",EDGE,{"disambiguationData":[OSD([subQ0]),TDD([makeQuery(id+"F6.imprint","IMPRINT",EDGE,{"disambiguationData":[TD([[makeQuery(id+"F6.imprint","INTERSECT",VERTEX,{"derivedFrom":[sQuery(id+"F6.wireOp",EDGE,"E46.right"),subQ0]}),-1.0]])],"derivedFrom":subQ0})])],"isStart":false});}
            var Q14;
            Q14=makeQuery(id+"F7.opExtrude","CAP_EDGE",EDGE,{"disambiguationData":[OSD([sQuery(id+"F6.wireOp",EDGE,"E47.right")])],"isStart":false});
            var Q15;
            {var subQ0=sQuery(id+"F6.wireOp",EDGE,"E47.bottom");Q15=makeQuery(id+"F7.opExtrude","CAP_EDGE",EDGE,{"disambiguationData":[OSD([subQ0]),TDD([makeQuery(id+"F6.imprint","IMPRINT",EDGE,{"disambiguationData":[TD([[makeQuery(id+"F6.imprint","INTERSECT",VERTEX,{"derivedFrom":[sQuery(id+"F6.wireOp",EDGE,"E46.right"),subQ0]}),-1.0]])],"derivedFrom":subQ0})])],"isStart":false});}
            var Q16;
            Q16=makeQuery(id+"F7.opExtrude","CAP_EDGE",EDGE,{"disambiguationData":[OSD([sQuery(id+"F6.wireOp",EDGE,"E46.top")])],"isStart":false});
            var Q17;
            Q17=makeQuery(id+"F7.opExtrude","CAP_EDGE",EDGE,{"disambiguationData":[OSD([sQuery(id+"F6.wireOp",EDGE,"E47.left")])],"isStart":false});
            var Q18;
            {var subQ0=sQuery(id+"F6.wireOp",EDGE,"E47.bottom");Q18=makeQuery(id+"F7.opExtrude","CAP_EDGE",EDGE,{"disambiguationData":[OSD([subQ0]),TDD([makeQuery(id+"F6.imprint","IMPRINT",EDGE,{"disambiguationData":[TD([[makeQuery(id+"F6.imprint","INTERSECT",VERTEX,{"derivedFrom":[sQuery(id+"F6.wireOp",EDGE,"E46.left"),subQ0]}),1.0]])],"derivedFrom":subQ0})])],"isStart":false});}
            var Q19;
            {var subQ0=sQuery(id+"F6.wireOp",EDGE,"E46.left");Q19=makeQuery(id+"F7.opExtrude","CAP_EDGE",EDGE,{"disambiguationData":[OSD([subQ0]),TDD([makeQuery(id+"F6.imprint","IMPRINT",EDGE,{"disambiguationData":[TD([[makeQuery(id+"F6.imprint","INTERSECT",VERTEX,{"derivedFrom":[subQ0,sQuery(id+"F6.wireOp",EDGE,"E47.bottom")]}),-1.0]])],"derivedFrom":subQ0})])],"isStart":false});}
            var Q20;
            {var subQ0=sQuery(id+"F6.wireOp",EDGE,"E47.top");Q20=makeQuery(id+"F7.opExtrude","CAP_EDGE",EDGE,{"disambiguationData":[OSD([subQ0]),TDD([makeQuery(id+"F6.imprint","IMPRINT",EDGE,{"disambiguationData":[TD([[makeQuery(id+"F6.imprint","INTERSECT",VERTEX,{"derivedFrom":[sQuery(id+"F6.wireOp",EDGE,"E46.left"),subQ0]}),1.0]])],"derivedFrom":subQ0})])],"isStart":false});}
            var Q21;
            {var subQ0=sQuery(id+"F6.wireOp",EDGE,"E46.left");var subQ1=sQuery(id+"F2.wireOp",EDGE,"E4.bottom");Q21=makeQuery(id+"F7.opExtrude","CAP_EDGE",EDGE,{"disambiguationData":[OSD([subQ0]),TDD([makeQuery(id+"F6.imprint","IMPRINT",EDGE,{"disambiguationData":[TD([[makeQuery(id+"F6.imprint","INTERSECT",VERTEX,{"derivedFrom":[makeQuery(id+"F3.boolean.opBoolean","COPY",EDGE,{"derivedFrom":makeQuery(id+"F3.opExtrude","CAP_EDGE",EDGE,{"disambiguationData":[OSD([subQ1]),TDD([makeQuery(id+"F2.imprint","IMPRINT",EDGE,{"disambiguationData":[TD([[makeQuery(id+"F2.imprint","INTERSECT",VERTEX,{"derivedFrom":[subQ1,sQuery(id+"F2.wireOp",EDGE,"E20")]}),-1.0]])],"derivedFrom":subQ1})])],"isStart":true})}),sQuery(id+"F6.wireOp",EDGE,"E46.bottom"),subQ0]}),1.0]])],"derivedFrom":subQ0})])],"isStart":false});}
            var Q22;
            Q22=makeQuery(id+"F7.opExtrude","CAP_EDGE",EDGE,{"disambiguationData":[OSD([sQuery(id+"F6.wireOp",EDGE,"E46.bottom")])],"isStart":false});
            var Q23;
            Q23=makeQuery(id+"F7.opExtrude","CAP_FACE",FACE,{"disambiguationData":[OSD([sQuery(id+"F6.wireOp",EDGE,"E46.bottom"),sQuery(id+"F6.wireOp",EDGE,"E46.top"),sQuery(id+"F6.wireOp",EDGE,"E46.left"),sQuery(id+"F6.wireOp",EDGE,"E46.right"),sQuery(id+"F6.wireOp",EDGE,"E47.bottom"),sQuery(id+"F6.wireOp",EDGE,"E47.top"),sQuery(id+"F6.wireOp",EDGE,"E47.left"),sQuery(id+"F6.wireOp",EDGE,"E47.right")])],"isStart":false});
            var Q24;
            {var subQ0=sQuery(id+"F6.wireOp",EDGE,"E49.left");Q24=makeQuery(id+"F7.opExtrude","CAP_EDGE",EDGE,{"disambiguationData":[OSD([subQ0]),TDD([makeQuery(id+"F6.imprint","IMPRINT",EDGE,{"disambiguationData":[TD([[makeQuery(id+"F6.imprint","INTERSECT",VERTEX,{"derivedFrom":[sQuery(id+"F6.wireOp",EDGE,"E48.bottom"),subQ0]}),-1.0]])],"derivedFrom":subQ0})])],"isStart":false});}
            var Q25;
            {var subQ0=sQuery(id+"F6.wireOp",EDGE,"E49.left");Q25=makeQuery(id+"F7.opExtrude","CAP_EDGE",EDGE,{"disambiguationData":[OSD([subQ0]),TDD([makeQuery(id+"F6.imprint","IMPRINT",EDGE,{"disambiguationData":[TD([[makeQuery(id+"F6.imprint","INTERSECT",VERTEX,{"derivedFrom":[sQuery(id+"F6.wireOp",EDGE,"E48.top"),subQ0]}),1.0]])],"derivedFrom":subQ0})])],"isStart":false});}
            var Q26;
            Q26=makeQuery(id+"F7.opExtrude","CAP_EDGE",EDGE,{"disambiguationData":[OSD([sQuery(id+"F6.wireOp",EDGE,"E49.bottom")])],"isStart":false});
            var Q27;
            {var subQ0=sQuery(id+"F6.wireOp",EDGE,"E49.right");Q27=makeQuery(id+"F7.opExtrude","CAP_EDGE",EDGE,{"disambiguationData":[OSD([subQ0]),TDD([makeQuery(id+"F6.imprint","IMPRINT",EDGE,{"disambiguationData":[TD([[makeQuery(id+"F6.imprint","INTERSECT",VERTEX,{"derivedFrom":[sQuery(id+"F6.wireOp",EDGE,"E48.top"),subQ0]}),1.0]])],"derivedFrom":subQ0})])],"isStart":false});}
            var Q28;
            {var subQ0=sQuery(id+"F6.wireOp",EDGE,"E48.top");Q28=makeQuery(id+"F7.opExtrude","CAP_EDGE",EDGE,{"disambiguationData":[OSD([subQ0]),TDD([makeQuery(id+"F6.imprint","IMPRINT",EDGE,{"disambiguationData":[TD([[makeQuery(id+"F6.imprint","INTERSECT",VERTEX,{"derivedFrom":[subQ0,sQuery(id+"F6.wireOp",EDGE,"E49.right")]}),1.0]])],"derivedFrom":subQ0})])],"isStart":false});}
            var Q29;
            Q29=makeQuery(id+"F7.opExtrude","CAP_EDGE",EDGE,{"disambiguationData":[OSD([sQuery(id+"F6.wireOp",EDGE,"E48.left")])],"isStart":false});
            var Q30;
            {var subQ0=sQuery(id+"F6.wireOp",EDGE,"E48.bottom");Q30=makeQuery(id+"F7.opExtrude","CAP_EDGE",EDGE,{"disambiguationData":[OSD([subQ0]),TDD([makeQuery(id+"F6.imprint","IMPRINT",EDGE,{"disambiguationData":[TD([[makeQuery(id+"F6.imprint","INTERSECT",VERTEX,{"derivedFrom":[subQ0,sQuery(id+"F6.wireOp",EDGE,"E49.right")]}),1.0]])],"derivedFrom":subQ0})])],"isStart":false});}
            var Q31;
            {var subQ0=sQuery(id+"F6.wireOp",EDGE,"E49.right");Q31=makeQuery(id+"F7.opExtrude","CAP_EDGE",EDGE,{"disambiguationData":[OSD([subQ0]),TDD([makeQuery(id+"F6.imprint","IMPRINT",EDGE,{"disambiguationData":[TD([[makeQuery(id+"F6.imprint","INTERSECT",VERTEX,{"derivedFrom":[sQuery(id+"F6.wireOp",EDGE,"E48.bottom"),subQ0]}),-1.0]])],"derivedFrom":subQ0})])],"isStart":false});}
            var Q32;
            Q32=makeQuery(id+"F7.opExtrude","CAP_EDGE",EDGE,{"disambiguationData":[OSD([sQuery(id+"F6.wireOp",EDGE,"E49.top")])],"isStart":false});
            var Q33;
            {var subQ0=sQuery(id+"F6.wireOp",EDGE,"E48.bottom");Q33=makeQuery(id+"F7.opExtrude","CAP_EDGE",EDGE,{"disambiguationData":[OSD([subQ0]),TDD([makeQuery(id+"F6.imprint","IMPRINT",EDGE,{"disambiguationData":[TD([[makeQuery(id+"F6.imprint","INTERSECT",VERTEX,{"derivedFrom":[subQ0,sQuery(id+"F6.wireOp",EDGE,"E49.left")]}),-1.0]])],"derivedFrom":subQ0})])],"isStart":false});}
            var Q34;
            {var subQ0=sQuery(id+"F6.wireOp",EDGE,"E48.top");Q34=makeQuery(id+"F7.opExtrude","CAP_EDGE",EDGE,{"disambiguationData":[OSD([subQ0]),TDD([makeQuery(id+"F6.imprint","IMPRINT",EDGE,{"disambiguationData":[TD([[makeQuery(id+"F6.imprint","INTERSECT",VERTEX,{"derivedFrom":[subQ0,sQuery(id+"F6.wireOp",EDGE,"E49.left")]}),-1.0]])],"derivedFrom":subQ0})])],"isStart":false});}
            var Q35;
            Q35=makeQuery(id+"F7.opExtrude","CAP_EDGE",EDGE,{"disambiguationData":[OSD([sQuery(id+"F6.wireOp",EDGE,"E41.left")])],"isStart":false});
            var Q36;
            {var subQ0=sQuery(id+"F6.wireOp",EDGE,"E51.bottom");Q36=makeQuery(id+"F7.opExtrude","CAP_EDGE",EDGE,{"disambiguationData":[OSD([subQ0]),TDD([makeQuery(id+"F6.imprint","IMPRINT",EDGE,{"disambiguationData":[TD([[makeQuery(id+"F6.imprint","INTERSECT",VERTEX,{"derivedFrom":[sQuery(id+"F6.wireOp",EDGE,"E50.right"),subQ0]}),1.0],[makeQuery(id+"F6.imprint","INTERSECT",VERTEX,{"derivedFrom":[sQuery(id+"F6.wireOp",EDGE,"E40.top"),subQ0,sQuery(id+"F6.wireOp",EDGE,"E51.right")]}),-1.0]])],"derivedFrom":subQ0})])],"isStart":false});}
            var Q37;
            {var subQ0=sQuery(id+"F6.wireOp",EDGE,"E50.right");Q37=makeQuery(id+"F7.opExtrude","CAP_EDGE",EDGE,{"disambiguationData":[OSD([subQ0]),TDD([makeQuery(id+"F6.imprint","IMPRINT",EDGE,{"disambiguationData":[TD([[makeQuery(id+"F6.imprint","INTERSECT",VERTEX,{"derivedFrom":[subQ0,sQuery(id+"F6.wireOp",EDGE,"E51.bottom")]}),-1.0]])],"derivedFrom":subQ0})])],"isStart":false});}
            var Q38;
            Q38=makeQuery(id+"F7.opExtrude","CAP_EDGE",EDGE,{"disambiguationData":[OSD([sQuery(id+"F6.wireOp",EDGE,"E39.bottom")])],"isStart":false});
            var Q39;
            {var subQ0=sQuery(id+"F6.wireOp",EDGE,"E50.left");var subQ1=sQuery(id+"F2.wireOp",EDGE,"E12.top");Q39=makeQuery(id+"F7.opExtrude","CAP_EDGE",EDGE,{"disambiguationData":[OSD([subQ0]),TDD([makeQuery(id+"F6.imprint","IMPRINT",EDGE,{"disambiguationData":[TD([[makeQuery(id+"F6.imprint","INTERSECT",VERTEX,{"derivedFrom":[makeQuery(id+"F3.boolean.opBoolean","COPY",EDGE,{"derivedFrom":makeQuery(id+"F3.opExtrude","CAP_EDGE",EDGE,{"disambiguationData":[OSD([subQ1]),TDD([makeQuery(id+"F2.imprint","IMPRINT",EDGE,{"disambiguationData":[TD([[makeQuery(id+"F2.imprint","INTERSECT",VERTEX,{"derivedFrom":[sQuery(id+"F2.wireOp",EDGE,"E8.right"),subQ1]}),-1.0]])],"derivedFrom":subQ1})])],"isStart":true})}),sQuery(id+"F6.wireOp",EDGE,"E39.left"),sQuery(id+"F6.wireOp",EDGE,"E39.bottom"),subQ0]}),-1.0],[makeQuery(id+"F6.imprint","INTERSECT",VERTEX,{"derivedFrom":[subQ0,sQuery(id+"F6.wireOp",EDGE,"E51.bottom")]}),1.0]])],"derivedFrom":subQ0})])],"isStart":false});}
            var Q40;
            {var subQ0=sQuery(id+"F6.wireOp",EDGE,"E51.bottom");var subQ1=sQuery(id+"F2.wireOp",EDGE,"E8.right");Q40=makeQuery(id+"F7.opExtrude","CAP_EDGE",EDGE,{"disambiguationData":[OSD([subQ0]),TDD([makeQuery(id+"F6.imprint","IMPRINT",EDGE,{"disambiguationData":[TD([[makeQuery(id+"F6.imprint","INTERSECT",VERTEX,{"derivedFrom":[makeQuery(id+"F3.boolean.opBoolean","COPY",EDGE,{"derivedFrom":makeQuery(id+"F3.opExtrude","CAP_EDGE",EDGE,{"disambiguationData":[OSD([subQ1]),TDD([makeQuery(id+"F2.imprint","IMPRINT",EDGE,{"disambiguationData":[TD([[makeQuery(id+"F2.imprint","INTERSECT",VERTEX,{"derivedFrom":[subQ1,sQuery(id+"F2.wireOp",EDGE,"E12.top")]}),-1.0]])],"derivedFrom":subQ1})])],"isStart":true})}),subQ0,sQuery(id+"F6.wireOp",EDGE,"E51.left")]}),1.0],[makeQuery(id+"F6.imprint","INTERSECT",VERTEX,{"derivedFrom":[sQuery(id+"F6.wireOp",EDGE,"E50.left"),subQ0]}),-1.0]])],"derivedFrom":subQ0})])],"isStart":false});}
            var Q41;
            Q41=makeQuery(id+"F7.opExtrude","CAP_EDGE",EDGE,{"disambiguationData":[OSD([sQuery(id+"F6.wireOp",EDGE,"E51.left")])],"isStart":false});
            var Q42;
            {var subQ0=sQuery(id+"F6.wireOp",EDGE,"E50.left");var subQ1=sQuery(id+"F2.wireOp",EDGE,"E4.top");Q42=makeQuery(id+"F7.opExtrude","CAP_EDGE",EDGE,{"disambiguationData":[OSD([subQ0]),TDD([makeQuery(id+"F6.imprint","IMPRINT",EDGE,{"disambiguationData":[TD([[makeQuery(id+"F6.imprint","INTERSECT",VERTEX,{"derivedFrom":[makeQuery(id+"F3.boolean.opBoolean","COPY",EDGE,{"derivedFrom":makeQuery(id+"F3.opExtrude","CAP_EDGE",EDGE,{"disambiguationData":[OSD([subQ1]),TDD([makeQuery(id+"F2.imprint","IMPRINT",EDGE,{"disambiguationData":[TD([[makeQuery(id+"F2.imprint","INTERSECT",VERTEX,{"derivedFrom":[subQ1,sQuery(id+"F2.wireOp",EDGE,"E8.right")]}),-1.0]])],"derivedFrom":subQ1})])],"isStart":true})}),sQuery(id+"F6.wireOp",EDGE,"E50.bottom"),subQ0]}),1.0],[makeQuery(id+"F6.imprint","INTERSECT",VERTEX,{"derivedFrom":[subQ0,sQuery(id+"F6.wireOp",EDGE,"E51.top")]}),-1.0]])],"derivedFrom":subQ0})])],"isStart":false});}
            var Q43;
            {var subQ0=sQuery(id+"F6.wireOp",EDGE,"E51.top");var subQ1=sQuery(id+"F2.wireOp",EDGE,"E8.right");Q43=makeQuery(id+"F7.opExtrude","CAP_EDGE",EDGE,{"disambiguationData":[OSD([subQ0]),TDD([makeQuery(id+"F6.imprint","IMPRINT",EDGE,{"disambiguationData":[TD([[makeQuery(id+"F6.imprint","INTERSECT",VERTEX,{"derivedFrom":[makeQuery(id+"F3.boolean.opBoolean","COPY",EDGE,{"derivedFrom":makeQuery(id+"F3.opExtrude","CAP_EDGE",EDGE,{"disambiguationData":[OSD([subQ1]),TDD([makeQuery(id+"F2.imprint","IMPRINT",EDGE,{"disambiguationData":[TD([[makeQuery(id+"F2.imprint","INTERSECT",VERTEX,{"derivedFrom":[sQuery(id+"F2.wireOp",EDGE,"E4.top"),subQ1]}),1.0]])],"derivedFrom":subQ1})])],"isStart":true})}),subQ0,sQuery(id+"F6.wireOp",EDGE,"E51.left")]}),1.0],[makeQuery(id+"F6.imprint","INTERSECT",VERTEX,{"derivedFrom":[sQuery(id+"F6.wireOp",EDGE,"E50.left"),subQ0]}),-1.0]])],"derivedFrom":subQ0})])],"isStart":false});}
            var Q44;
            Q44=makeQuery(id+"F7.opExtrude","CAP_EDGE",EDGE,{"disambiguationData":[OSD([sQuery(id+"F6.wireOp",EDGE,"E50.bottom")])],"isStart":false});
            var Q45;
            {var subQ0=sQuery(id+"F6.wireOp",EDGE,"E51.top");Q45=makeQuery(id+"F7.opExtrude","CAP_EDGE",EDGE,{"disambiguationData":[OSD([subQ0]),TDD([makeQuery(id+"F6.imprint","IMPRINT",EDGE,{"disambiguationData":[TD([[makeQuery(id+"F6.imprint","INTERSECT",VERTEX,{"derivedFrom":[makeQuery(id+"F3.boolean.opBoolean","COPY",EDGE,{"derivedFrom":makeQuery(id+"F3.opExtrude","CAP_EDGE",EDGE,{"disambiguationData":[OSD([sQuery(id+"F2.wireOp",EDGE,"E29.left")])],"isStart":true})}),sQuery(id+"F6.wireOp",EDGE,"E40.bottom"),subQ0,sQuery(id+"F6.wireOp",EDGE,"E51.right")]}),-1.0],[makeQuery(id+"F6.imprint","INTERSECT",VERTEX,{"derivedFrom":[sQuery(id+"F6.wireOp",EDGE,"E50.right"),subQ0]}),1.0]])],"derivedFrom":subQ0})])],"isStart":false});}
            var Q46;
            Q46=makeQuery(id+"F7.opExtrude","CAP_EDGE",EDGE,{"disambiguationData":[OSD([sQuery(id+"F6.wireOp",EDGE,"E51.right")])],"isStart":false});
            var Q47;
            {var subQ0=sQuery(id+"F6.wireOp",EDGE,"E50.right");var subQ1=sQuery(id+"F2.wireOp",EDGE,"E4.top");Q47=makeQuery(id+"F7.opExtrude","CAP_EDGE",EDGE,{"disambiguationData":[OSD([subQ0]),TDD([makeQuery(id+"F6.imprint","IMPRINT",EDGE,{"disambiguationData":[TD([[makeQuery(id+"F6.imprint","INTERSECT",VERTEX,{"derivedFrom":[makeQuery(id+"F3.boolean.opBoolean","COPY",EDGE,{"derivedFrom":makeQuery(id+"F3.opExtrude","CAP_EDGE",EDGE,{"disambiguationData":[OSD([subQ1]),TDD([makeQuery(id+"F2.imprint","IMPRINT",EDGE,{"disambiguationData":[TD([[makeQuery(id+"F2.imprint","INTERSECT",VERTEX,{"derivedFrom":[subQ1,sQuery(id+"F2.wireOp",EDGE,"E21.top"),sQuery(id+"F2.wireOp",EDGE,"E21.left")]}),-1.0]])],"derivedFrom":subQ1})])],"isStart":true})}),sQuery(id+"F6.wireOp",EDGE,"E50.bottom"),subQ0]}),1.0]])],"derivedFrom":subQ0})])],"isStart":false});}
            chamfer(context, id + "F8", {"entities" : qUnion([Q0, Q1, Q2, Q3, Q4, Q5, Q6, Q7, Q8, Q9, Q10, Q11, Q12, Q13, Q14, Q15, Q16, Q17, Q18, Q19, Q20, Q21, Q22, Q23, Q24, Q25, Q26, Q27, Q28, Q29, Q30, Q31, Q32, Q33, Q34, Q35, Q36, Q37, Q38, Q39, Q40, Q41, Q42, Q43, Q44, Q45, Q46, Q47]), "width" : 1.27 * mm, "tangentPropagation" : true});
        }
        {
            var Q0;
            Q0=makeQuery(id+"F1.opExtrude","CAP_FACE",FACE,{"disambiguationData":[OSD([sQuery(id+"F0.wireOp",EDGE,"E1")])],"isStart":false});
            var sketch = newSketch(context, id + "F9", { "sketchPlane" : qUnion([Q0])});
            skLineSegment(sketch, "E52.bottom", {"start": v(13.67, 49.13) * mm, "end": v(-6.44, 49.13) * mm});
            skLineSegment(sketch, "E52.left", {"start": v(13.67, 49.13) * mm, "end": v(13.67, 59.18) * mm});
            skLineSegment(sketch, "E52.right", {"start": v(-6.44, 49.13) * mm, "end": v(-6.44, 59.18) * mm});
            skPoint(sketch, "E52.middle", {"position": v(3.62, 59.18) * mm});
            skPoint(sketch, "E52.top.end.orphan", {"position": v(-6.44, 69.24) * mm});
            skPoint(sketch, "E53.end.orphan", {"position": v(13.67, 69.24) * mm});
            skSolve(sketch);
        }
        {
            var Q0;
            {var subQ0=sQuery(id+"F9.wireOp",EDGE,"E52.right");Q0=makeQuery(id+"F9.imprint","IMPRINT",FACE,{"disambiguationData":[TD([[makeQuery(id+"F9.imprint","IMPRINT",EDGE,{"derivedFrom":subQ0}),-1.0]])]});}
            var Q1;
            {var subQ0=sQuery(id+"F9.wireOp",EDGE,"E52.left");Q1=makeQuery(id+"F9.imprint","IMPRINT",FACE,{"disambiguationData":[TD([[makeQuery(id+"F9.imprint","IMPRINT",EDGE,{"derivedFrom":subQ0}),1.0]])]});}
            extrude(context, id + "F10", {"entities" : qUnion([Q0, Q1]), "depth" : -6.35 * mm, "offsetDistance" : 25.4 * mm});
        }
    });
